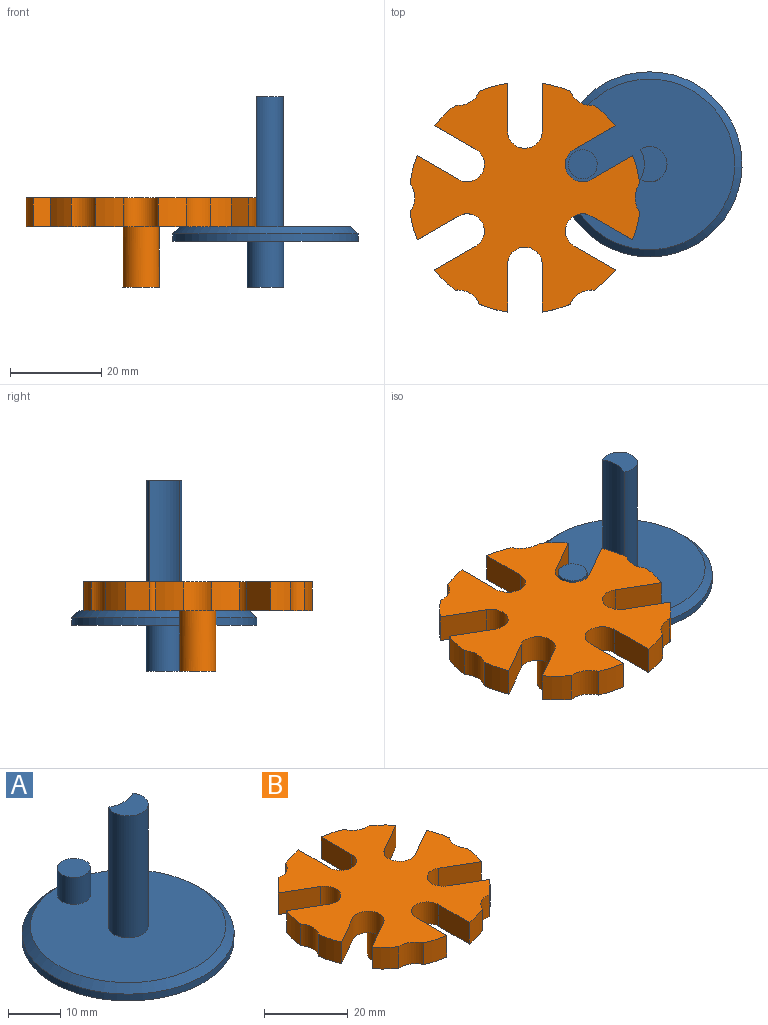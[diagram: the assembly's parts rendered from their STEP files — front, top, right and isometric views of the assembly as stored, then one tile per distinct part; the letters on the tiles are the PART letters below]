
ASSEMBLY  parts=2 mates=1
PART A: 11 faces, bbox 40.6x40.6x41.9 mm
  f0: cylinder r=6.69mm len=28.58mm, axis (0,0,-1), area 198mm2, adj f2,f4,f5
  f1: cylinder r=20.32mm len=40.64mm, axis (0,0,-1), area 202.7mm2, adj f3,f8
  f2: plane 37.47x37.47mm, normal (0,0,1), area 1036.6mm2, adj f0,f4,f6,f8
  f3: plane 40.64x40.64mm, normal (0,0,-1), area 1247.2mm2, adj f1,f9
  f4: cylinder r=3.86mm len=28.58mm, axis (0,0,-1), area 465.7mm2, adj f0,f2,f5
  f5: plane 7.72x5.85mm, normal (0,0,1), area 34.1mm2, adj f0,f4
  f6: cylinder r=3.17mm len=6.35mm, axis (0,0,-1), area 126.7mm2, adj f2,f7
  f7: plane 6.35x6.35mm, normal (0,0,1), area 31.7mm2, adj f6
  f8: cone r=18.73mm half-angle=45deg, axis (0,0,-1), area 275.4mm2, adj f1,f2
  f9: cylinder r=3.99mm len=10.16mm, axis (0,0,1), area 254.6mm2, adj f3,f10
  f10: plane 7.98x7.98mm, normal (0,0,-1), area 50mm2, adj f9
PART B: 40 faces, bbox 50.4x50.2x19.7 mm
  f0: plane 9.06x6.35mm, normal (-0.5,-0.87,0), area 66.4mm2, adj f1,f35,f36,f37
  f1: cylinder r=3.81mm len=7.11mm, axis (0,0,-1), area 76mm2, adj f0,f2,f36,f37
  f2: plane 9.06x6.35mm, normal (0.5,0.87,0), area 66.4mm2, adj f1,f3,f36,f37
  f3: cylinder r=25.4mm len=6.35mm, axis (0,0,-1), area 40.5mm2, adj f2,f4,f36,f37
  f4: cylinder r=5.13mm len=6.35mm, axis (0,0,-1), area 42mm2, adj f3,f5,f36,f37
  f5: cylinder r=25.4mm len=6.35mm, axis (0,0,-1), area 40.5mm2, adj f4,f6,f36,f37
  f6: plane 9.06x6.35mm, normal (0.5,-0.87,0), area 66.4mm2, adj f5,f7,f36,f37
  f7: cylinder r=3.81mm len=7.11mm, axis (0,0,-1), area 76mm2, adj f6,f8,f36,f37
  f8: plane 9.06x6.35mm, normal (-0.5,0.87,0), area 66.4mm2, adj f7,f9,f36,f37
  f9: cylinder r=25.4mm len=6.35mm, axis (0,0,-1), area 40.5mm2, adj f8,f10,f36,f37
  f10: cylinder r=5.13mm len=6.35mm, axis (0,0,-1), area 42mm2, adj f9,f11,f36,f37
  f11: cylinder r=25.4mm len=6.35mm, axis (0,0,-1), area 40.5mm2, adj f10,f12,f36,f37
  f12: plane 10.46x6.35mm, normal (1,0,0), area 66.4mm2, adj f11,f13,f36,f37
  f13: cylinder r=3.81mm len=7.62mm, axis (0,0,-1), area 76mm2, adj f12,f14,f36,f37
  f14: plane 10.46x6.35mm, normal (-1,0,0), area 66.4mm2, adj f13,f15,f36,f37
  f15: cylinder r=25.4mm len=6.35mm, axis (0,0,-1), area 40.5mm2, adj f14,f16,f36,f37
  f16: cylinder r=5.13mm len=6.35mm, axis (0,0,-1), area 42mm2, adj f15,f17,f36,f37
  f17: cylinder r=25.4mm len=6.35mm, axis (0,0,-1), area 40.5mm2, adj f16,f18,f36,f37
  f18: plane 9.06x6.35mm, normal (0.5,0.87,0), area 66.4mm2, adj f17,f19,f36,f37
  f19: cylinder r=3.81mm len=7.11mm, axis (0,0,-1), area 76mm2, adj f18,f20,f36,f37
  f20: plane 9.06x6.35mm, normal (-0.5,-0.87,0), area 66.4mm2, adj f19,f21,f36,f37
  f21: cylinder r=25.4mm len=6.35mm, axis (0,0,-1), area 40.5mm2, adj f20,f22,f36,f37
  f22: cylinder r=5.13mm len=6.35mm, axis (0,0,-1), area 42mm2, adj f21,f23,f36,f37
  f23: cylinder r=25.4mm len=6.35mm, axis (0,0,-1), area 40.5mm2, adj f22,f24,f36,f37
  f24: plane 9.06x6.35mm, normal (-0.5,0.87,0), area 66.4mm2, adj f23,f25,f36,f37
  f25: cylinder r=3.81mm len=7.11mm, axis (0,0,-1), area 76mm2, adj f24,f26,f36,f37
  f26: plane 9.06x6.35mm, normal (0.5,-0.87,0), area 66.4mm2, adj f25,f27,f36,f37
  f27: cylinder r=25.4mm len=6.35mm, axis (0,0,-1), area 40.5mm2, adj f26,f28,f36,f37
  f28: cylinder r=5.13mm len=6.35mm, axis (0,0,-1), area 42mm2, adj f27,f29,f36,f37
  f29: cylinder r=25.4mm len=6.35mm, axis (0,0,-1), area 40.5mm2, adj f28,f30,f36,f37
  f30: plane 10.46x6.35mm, normal (-1,0,0), area 66.4mm2, adj f29,f31,f36,f37
  f31: cylinder r=3.81mm len=7.62mm, axis (0,0,-1), area 76mm2, adj f30,f32,f36,f37
  f32: plane 10.46x6.35mm, normal (1,0,0), area 66.4mm2, adj f31,f33,f36,f37
  f33: cylinder r=25.4mm len=6.35mm, axis (0,0,-1), area 40.5mm2, adj f32,f34,f36,f37
  f34: cylinder r=5.13mm len=6.35mm, axis (0,0,-1), area 42mm2, adj f33,f35,f36,f37
  f35: cylinder r=25.4mm len=6.35mm, axis (0,0,-1), area 40.5mm2, adj f0,f34,f36,f37
  f36: plane 50.42x50.23mm, normal (0,0,1), area 1372.5mm2, adj f0,f1,f2,f3,f4,f5,f6,f7
  f37: plane 50.42x50.23mm, normal (0,0,-1), area 1322.6mm2, adj f0,f1,f2,f3,f4,f5,f6,f7
  f38: cylinder r=3.99mm len=13.34mm, axis (0,0,1), area 334.1mm2, adj f37,f39
  f39: plane 7.98x7.98mm, normal (0,0,-1), area 50mm2, adj f38
PLACE A rot(axis=(0,0,1),90deg) t=(-20.68,-7.98,8.52)mm
PLACE B t=(-48.03,-15.31,11.7)mm
MATE slider A.f6 <-> B.f25  axis (0,0,1) through (-35.34,-7.98,11.7)mm
